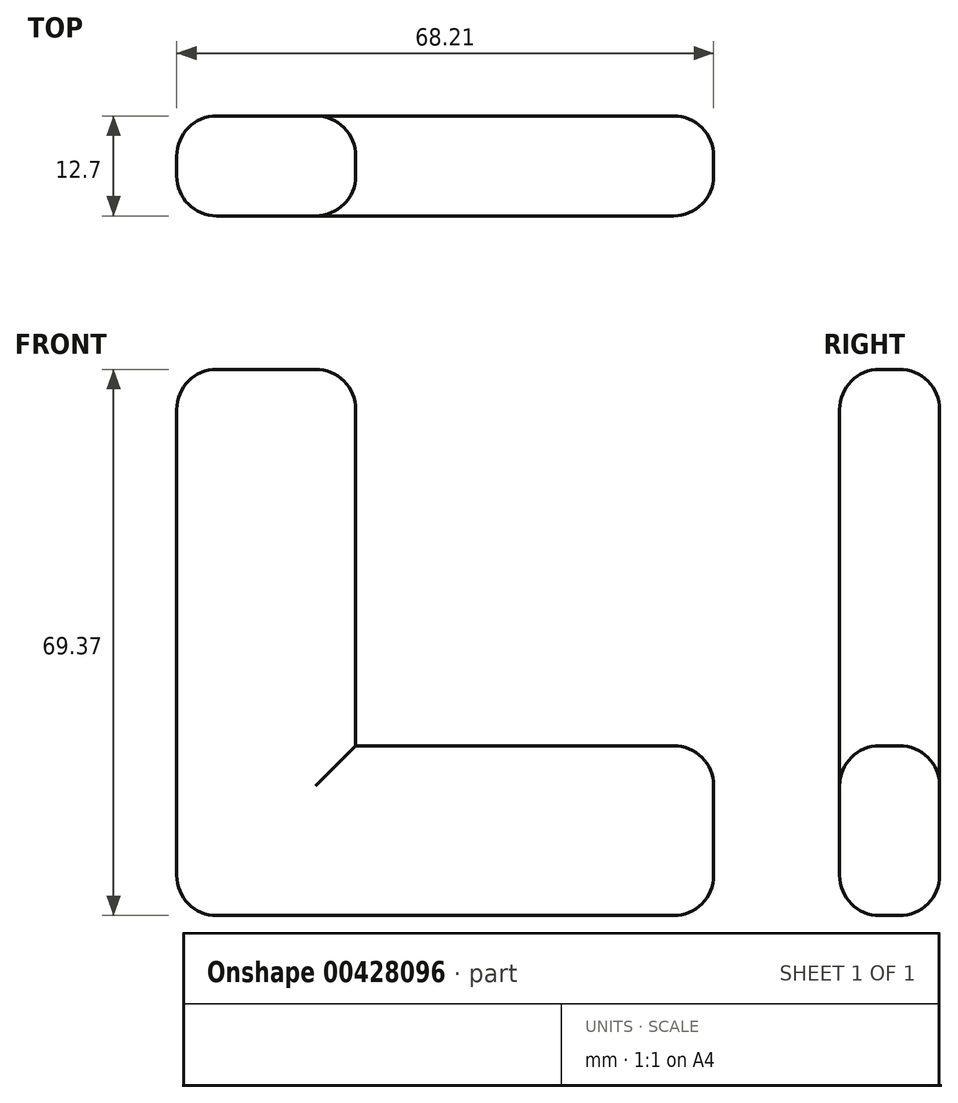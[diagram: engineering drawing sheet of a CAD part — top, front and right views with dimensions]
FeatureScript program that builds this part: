
annotation { "Feature Type Name" : "Feature", "Feature Type Description" : "" }
export const myFeature = defineFeature(function(context is Context, id is Id, definition is map)
    precondition{}
    {
        {
            var Q0;
            Q0=qCreatedBy(makeId("Front.planeOp"),FACE);
            var sketch = newSketch(context, id + "F0", { "sketchPlane" : qUnion([Q0])});
            skLineSegment(sketch, "E0", {"start": v(-38.77, 56.7) * mm, "end": v(-38.77, -12.68) * mm});
            skLineSegment(sketch, "E1", {"start": v(-38.77, -12.68) * mm, "end": v(29.44, -12.68) * mm});
            skLineSegment(sketch, "E2", {"start": v(29.44, -12.68) * mm, "end": v(29.44, 8.9) * mm});
            skLineSegment(sketch, "E3", {"start": v(29.44, 8.9) * mm, "end": v(-16.03, 8.9) * mm});
            skLineSegment(sketch, "E4", {"start": v(-16.03, 8.9) * mm, "end": v(-16.03, 56.7) * mm});
            skLineSegment(sketch, "E5", {"start": v(-16.03, 56.7) * mm, "end": v(-38.77, 56.7) * mm});
            skSolve(sketch);
        }
        {
            var Q0;
            Q0 = qSketchRegion(id + "F0", true);
            extrude(context, id + "F1", {"entities" : qUnion([Q0]), "depth" : 12.7 * mm});
        }
        {
            var Q0;
            Q0=makeQuery(id+"F1.opExtrude","CAP_EDGE",EDGE,{"disambiguationData":[OSD([sQuery(id+"F0.wireOp",EDGE,"E0")])],"isStart":false});
            var Q1;
            Q1=makeQuery(id+"F1.opExtrude","CAP_EDGE",EDGE,{"disambiguationData":[OSD([sQuery(id+"F0.wireOp",EDGE,"E5")])],"isStart":false});
            var Q2;
            Q2=makeQuery(id+"F1.opExtrude","CAP_EDGE",EDGE,{"disambiguationData":[OSD([sQuery(id+"F0.wireOp",EDGE,"E4")])],"isStart":false});
            var Q3;
            Q3=makeQuery(id+"F1.opExtrude","CAP_EDGE",EDGE,{"disambiguationData":[OSD([sQuery(id+"F0.wireOp",EDGE,"E3")])],"isStart":false});
            var Q4;
            Q4=makeQuery(id+"F1.opExtrude","CAP_EDGE",EDGE,{"disambiguationData":[OSD([sQuery(id+"F0.wireOp",EDGE,"E2")])],"isStart":false});
            var Q5;
            Q5=makeQuery(id+"F1.opExtrude","CAP_EDGE",EDGE,{"disambiguationData":[OSD([sQuery(id+"F0.wireOp",EDGE,"E1")])],"isStart":false});
            var Q6;
            Q6=makeQuery(id+"F1.opExtrude","SWEPT_EDGE",EDGE,{"disambiguationData":[OSD([sQuery(id+"F0.wireOp",EDGE,"E1"),sQuery(id+"F0.wireOp",EDGE,"E2")])]});
            var Q7;
            Q7=makeQuery(id+"F1.opExtrude","SWEPT_EDGE",EDGE,{"disambiguationData":[OSD([sQuery(id+"F0.wireOp",EDGE,"E2"),sQuery(id+"F0.wireOp",EDGE,"E3")])]});
            var Q8;
            Q8=makeQuery(id+"F1.opExtrude","SWEPT_EDGE",EDGE,{"disambiguationData":[OSD([sQuery(id+"F0.wireOp",EDGE,"E4"),sQuery(id+"F0.wireOp",EDGE,"E5")])]});
            var Q9;
            Q9=makeQuery(id+"F1.opExtrude","SWEPT_EDGE",EDGE,{"disambiguationData":[OSD([sQuery(id+"F0.wireOp",EDGE,"E0"),sQuery(id+"F0.wireOp",EDGE,"E5")])]});
            var Q10;
            Q10=makeQuery(id+"F1.opExtrude","SWEPT_EDGE",EDGE,{"disambiguationData":[OSD([sQuery(id+"F0.wireOp",EDGE,"E0"),sQuery(id+"F0.wireOp",EDGE,"E1")])]});
            fillet(context, id + "F2", {"entities" : qUnion([Q0, Q1, Q2, Q3, Q4, Q5, Q6, Q7, Q8, Q9, Q10]), "radius" : 5.08 * mm, "tangentPropagation" : true, "allowEdgeOverflow" : false});
        }
        {
            var Q0;
            Q0=makeQuery(id+"F1.opExtrude","CAP_EDGE",EDGE,{"disambiguationData":[OSD([sQuery(id+"F0.wireOp",EDGE,"E1")])],"isStart":true});
            fillet(context, id + "F3", {"entities" : qUnion([Q0]), "radius" : 5.08 * mm, "tangentPropagation" : true, "allowEdgeOverflow" : false});
        }
    });
